# Revit family: Sanitary_Wash-basins_DURAVIT-AG_235312-DuraSquare-Washbasin_туц
name_source: partatom
category: Plumbing Fixtures
units: mm (PartAtom-declared; Revit-internal decimal feet)

## family parameters
Cut with Voids When Loaded = Yes
Host = Face
Maintain Annotation Orientation = No
OmniClass Number = 23.31.13.00
OmniClass Title = Sinks
Part Type = Normal
Room Calculation Point = No
Round Connector Dimension = Use Diameter
Shared = No

## types (4) — shared parameters
Default Elevation = 1219 mm
Depth = 470 mm  [stored 1.54199 ft]
Diameter = 32 mm  [stored 0.104987 ft]
Height = 145 mm  [stored 0.475722 ft]
Installation instructions = https://pro.duravit.com
Manufacturer = Duravit
Material 1 = Duravit - Ceramic - 00 - White Alpin
Model = 235312 washbasin DuraCeram rectangular
Product Documentation Link = https://pro.duravit.com
Product Page URL = https://pro.duravit.com
Product data url = https://bimobject.com
URL = http://pro.duravit.com
Version = 1
Weight = 28.30 kg
Width = 1200 mm

## per-type parameters (varying)
| type | Description | z_tap holes 2D |
| Duravit DuraSquare Washbasin 1200 mm White High Gloss - 2353120041 | Duravit DuraSquare Washbasin 1200 mm White High Gloss, Tap hole platform, Number of faucet holes per wash area: 1 – 2353120041 | Yes |
| Duravit DuraSquare Washbasin 1200 mm White High Gloss - 2353120070 | Duravit DuraSquare Washbasin 1200 mm White High Gloss, Tap hole platform, Number of faucet holes per wash area: 0 – 2353120070 | No |
| Duravit DuraSquare Washbasin 1200 mm White High Gloss - 2353120071 | Duravit DuraSquare Washbasin 1200 mm White High Gloss, Tap hole platform, Number of faucet holes per wash area: 1, Ground – 2353120071 | Yes |
| Duravit DuraSquare Washbasin 1200 mm White High Gloss - 2353120079 | Duravit DuraSquare Washbasin 1200 mm White High Gloss, Tap hole platform, Number of faucet holes per wash area: 0, Ground – 2353120079 | No |

note: [stored X ft] marks values corroborated as IEEE doubles in the binary element streams (Revit-internal decimal feet)

## geometry (parser evidence)
native form markers: Sweep x3
no freeform markers — native parametric forms only
